# Revit family: O2UM-NRG
name_source: partatom
category: Mechanical Equipment
units: mm (PartAtom-declared; Revit-internal decimal feet)

## family parameters
Always vertical = Yes
Cut with Voids When Loaded = No
OmniClass Number = 23.40.40.11.17
OmniClass Title = Refrigerated Cases
Part Type = Normal
Room Calculation Point = No
Round Connector Dimension = Use Radius
Shared = No
Work Plane-Based = Yes

## types (4) — shared parameters
ANTI SWEAT HEATER AMPS = 0 A
BASE HEIGHT = 5 1/8"
BTU PER FOOT CONVENTIONAL = 1023
BTU PER FOOT PARALLEL = 948
CERTIFICATIONS = NSF 7, UL471, CSA
COIL REFRIGERATION CHARGE = 0.00 lb
CONTROL TYPE = T-STAT
DATE = 08/22/12
DEDICATED CIRCUIT = YES
DEFROST PHASE = 1
DEFROST TIME AND DURATION = 2 @ 60 MIN
DEFROST WATTAGE = 0 W
DIEBOARD HEIGHT = 0"
DISCHARGE AIR TEMPERATURE = 27 °F
DRAIN LINE CONNECTION = Drain Connection
DRAIN LINE DIAMETER = 2"
DRAIN LINE RADIUS = 1"
DRAIN PIPE TYPE = PVC
DRIP PAN PLUMB TYPE = HARD
Default Elevation = 48"
Description = MULTI DECK MERCHANDISER
ELECTRIC DEFROST = No
ELECTRICAL DEFROST VOLTAGE = 0 V
EVAPORATOR TEMPERATURE = 22 °F
FAN AMPS = 0 A
FAN CONNECTOR DESCRIPTION = FAN AND ANTI SWEAT CONNECTOR
FAN NUMBER OF POLES = 1
FAN TYPE = ECM
GROUND FAULT PROTECTION = NO
HEIGHT = 40 11/16"
HOT GAS DEFROST = No
ISOLATED GROUND REQUIRED = NO
Keynote = DAIRY/DELI/MEAT/PRODUCE/SEAFOOD
LED LIGHTING AMPS PER ROW = 0 A
LEGEND NUMBER = O2UM-NRG
LIGHT TYPE = T8 FLUORESCENT
LIGHTING CONNECTION DESCRIPTION = LIGHTING CONNECTOR
LIGHTING NUMBER OF POLES = 1
LIQUID LINE CONNECTION = LIQUID LINE CONNECTION
LIQUID LINE DIAMETER = 0"
LIQUID LINE RADIUS = 0"
Manufacturer = HILL PHOENIX
Model = O2UM-NRG
NUMBER OF WIRES = 3
PHASE = 1
POWER FACTOR = 1
PRESSURE REGULATOR = 0.00 psi
RECEPTICAL MOUNTING HEIGHT ABOVE FLOOR = 19 3/4"
REF PLANE FRONT BACK = 21 5/8"
REVERSE AIR DEFROST = No
SET BACK MODE FOR ENERGY CONSERVATION = NO
SHELVE 1 = Yes
SIZE OF COLD WATER HOOK UP = 0"
SIZE OF HOT WATER HOOK-UP = 0"
SUCTION LINE CONNECTION = SUCTION LINE CONNECTION
SUCTION LINE DIAMETER = 1"
SUCTION LINE RADIUS = 0"
T8 LIGHT OR LED LIGHT = Yes
TIME OFF DEFROST = Yes
TOEKICK HEIGHT = 5 1/2"
TOEKICK INSET = 1 1/2"
Tag Molding = <By Category>
URL = http://www.hillphoenix.com
VOLTAGE = 120 V
WATER LINE MOUNTING HEIGHT ABOVE FLOOR = 0"
WEIGHT = 0.00 lb
WIDTH = 43 1/4"
zero-valued in all types: CORNICE AND NOSE LIGHT ROWS

## per-type parameters (varying)
- 04': ANTI SWEAT APPARENT LOAD=17 VA; ANTI SWEAT HEATER WATTAGE=17 W; BTU ADD FOR LIGHTS=320; BTU ADD PER SHELF PER FOOT=80; CONVENTIONAL EVAPORATOR LOAD=4412; DEFROST AMPS=2 A; DRAIN PIPE LENGTH=12"; FAN AND ANTI SWEAT HEATER APPARENT LOAD=35 VA; FAN APPARENT LOAD=18 VA; FAN QUANTITY=2; FAN WATTAGE=9 W; LED LIGHTING AMPS=0 A; LED LIGHTING BTU ADD PER ROW=36; LED LIGHTING WATTAGE=12 W; LENGTH=48"; LENGTH FOR BTU=4; LIGHT AMPS=0 A; LIGHTING APPARENT LOAD=28 VA; LIGHTING WATTAGE=28 VA; PARALLEL EVAPORATOR LOAD=4112; REF PIPE LENGTH=22 9/16"; REF PLANE LEFT RIGHT=24"; SHELF LIGHT ROWS=1; SHELVE 2=No; SHELVE 3=No; SHELVE LENGTH=48"; T8 LIGHTING AMPS=0 A; T8 LIGHTING AMPS PER ROW=0 A; T8 LIGHTING BTU ADD PER ROW=80; T8 LIGHTING WATTAGE=28 W; TOTAL APPARENT FAN-LIGHT AND A/S LOAD=54 VA; TOTAL CASE AMPS=1 A; TOTAL CASE WATTAGE=54 W
- 06': ANTI SWEAT APPARENT LOAD=24 VA; ANTI SWEAT HEATER WATTAGE=24 W; BTU ADD FOR LIGHTS=720; BTU ADD PER SHELF PER FOOT=60; CONVENTIONAL EVAPORATOR LOAD=6858; DEFROST AMPS=3 A; DRAIN PIPE LENGTH=0"; FAN AND ANTI SWEAT HEATER APPARENT LOAD=42 VA; FAN APPARENT LOAD=18 VA; FAN QUANTITY=2; FAN WATTAGE=9 W; LED LIGHTING AMPS=0 A; LED LIGHTING BTU ADD PER ROW=27; LED LIGHTING WATTAGE=34 W; LENGTH=72"; LENGTH FOR BTU=6; LIGHT AMPS=1 A; LIGHTING APPARENT LOAD=89 VA; LIGHTING WATTAGE=89 VA; PARALLEL EVAPORATOR LOAD=6408; REF PIPE LENGTH=28 5/8"; REF PLANE LEFT RIGHT=36"; SHELF LIGHT ROWS=2; SHELVE 2=No; SHELVE 3=Yes; SHELVE LENGTH=36"; T8 LIGHTING AMPS=1 A; T8 LIGHTING AMPS PER ROW=0 A; T8 LIGHTING BTU ADD PER ROW=60; T8 LIGHTING WATTAGE=89 W; TOTAL APPARENT FAN-LIGHT AND A/S LOAD=122 VA; TOTAL CASE AMPS=1 A; TOTAL CASE WATTAGE=122 W
- 08': ANTI SWEAT APPARENT LOAD=30 VA; ANTI SWEAT HEATER WATTAGE=30 W; BTU ADD FOR LIGHTS=1280; BTU ADD PER SHELF PER FOOT=80; CONVENTIONAL EVAPORATOR LOAD=9464; DEFROST AMPS=4 A; DRAIN PIPE LENGTH=0"; FAN AND ANTI SWEAT HEATER APPARENT LOAD=58 VA; FAN APPARENT LOAD=28 VA; FAN QUANTITY=3; FAN WATTAGE=14 W; LED LIGHTING AMPS=0 A; LED LIGHTING BTU ADD PER ROW=36; LED LIGHTING WATTAGE=48 W; LENGTH=96"; LENGTH FOR BTU=8; LIGHT AMPS=1 A; LIGHTING APPARENT LOAD=113 VA; LIGHTING WATTAGE=113 VA; PARALLEL EVAPORATOR LOAD=8864; REF PIPE LENGTH=28 5/8"; REF PLANE LEFT RIGHT=48"; SHELF LIGHT ROWS=2; SHELVE 2=No; SHELVE 3=Yes; SHELVE LENGTH=48"; T8 LIGHTING AMPS=1 A; T8 LIGHTING AMPS PER ROW=0 A; T8 LIGHTING BTU ADD PER ROW=80; T8 LIGHTING WATTAGE=113 W; TOTAL APPARENT FAN-LIGHT AND A/S LOAD=157 VA; TOTAL CASE AMPS=1 A; TOTAL CASE WATTAGE=157 W
- 12': ANTI SWEAT APPARENT LOAD=46 VA; ANTI SWEAT HEATER WATTAGE=46 W; BTU ADD FOR LIGHTS=2880; BTU ADD PER SHELF PER FOOT=80; CONVENTIONAL EVAPORATOR LOAD=15156; DEFROST AMPS=6 A; DRAIN PIPE LENGTH=0"; FAN AND ANTI SWEAT HEATER APPARENT LOAD=83 VA; FAN APPARENT LOAD=37 VA; FAN QUANTITY=4; FAN WATTAGE=18 W; LED LIGHTING AMPS=1 A; LED LIGHTING BTU ADD PER ROW=36; LED LIGHTING WATTAGE=108 W; LENGTH=144"; LENGTH FOR BTU=12; LIGHT AMPS=2 A; LIGHTING APPARENT LOAD=252 VA; LIGHTING WATTAGE=252 VA; PARALLEL EVAPORATOR LOAD=14256; REF PIPE LENGTH=28 5/8"; REF PLANE LEFT RIGHT=72"; SHELF LIGHT ROWS=3; SHELVE 2=Yes; SHELVE 3=Yes; SHELVE LENGTH=48"; T8 LIGHTING AMPS=2 A; T8 LIGHTING AMPS PER ROW=1 A; T8 LIGHTING BTU ADD PER ROW=80; T8 LIGHTING WATTAGE=252 W; TOTAL APPARENT FAN-LIGHT AND A/S LOAD=316 VA; TOTAL CASE AMPS=3 A; TOTAL CASE WATTAGE=316 W

## geometry (parser evidence)
native form markers: Blend x2, Sweep x9
no freeform markers — native parametric forms only
